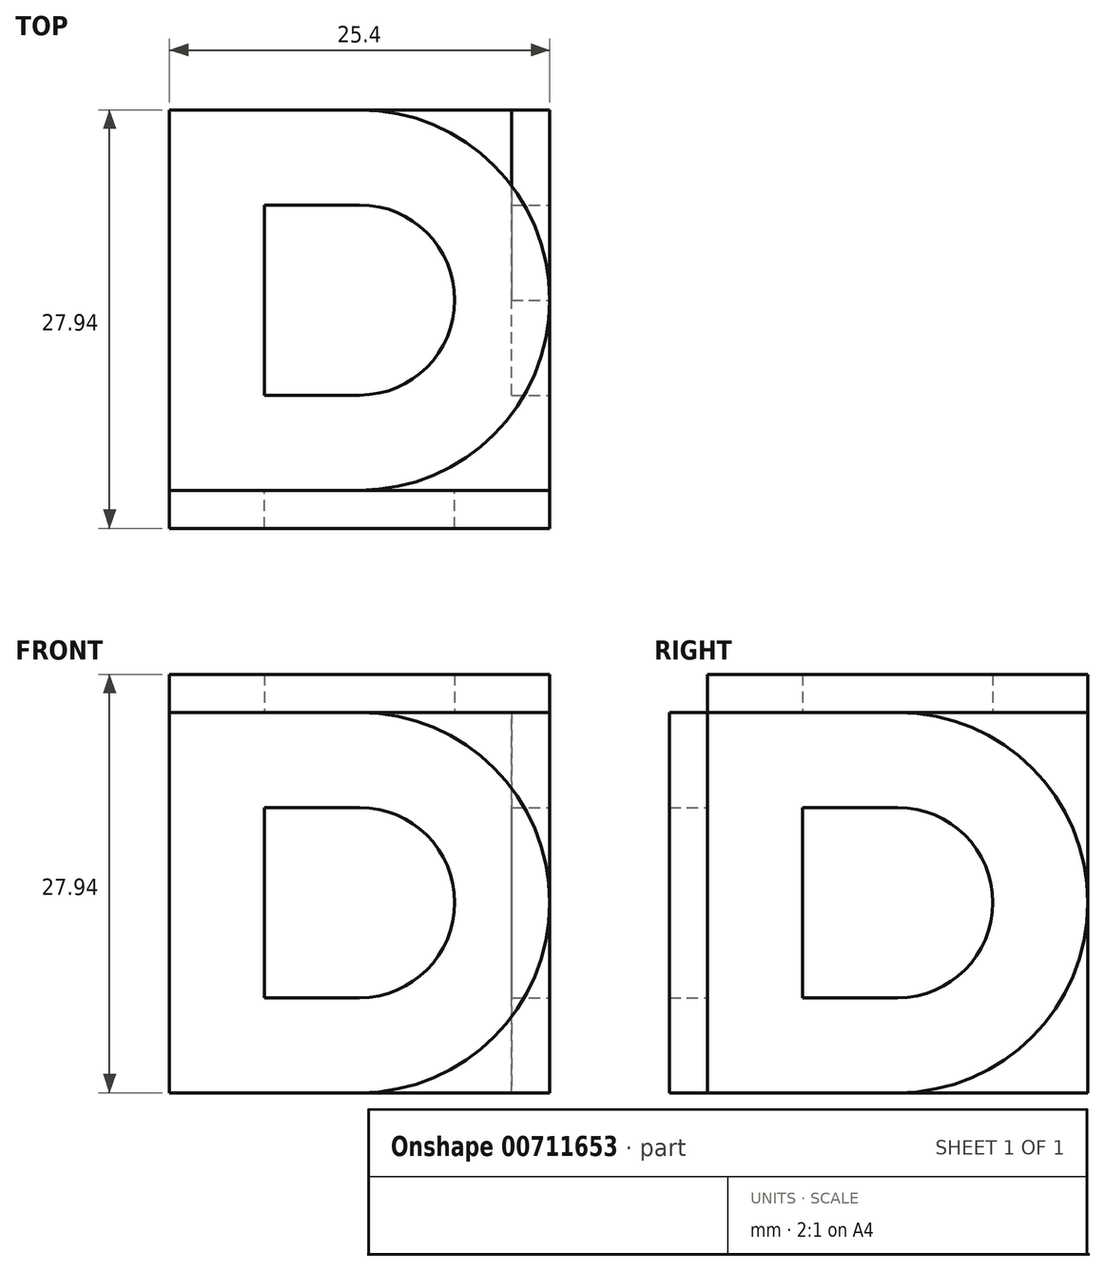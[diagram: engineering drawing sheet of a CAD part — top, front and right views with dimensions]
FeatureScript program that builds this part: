
annotation { "Feature Type Name" : "Feature", "Feature Type Description" : "" }
export const myFeature = defineFeature(function(context is Context, id is Id, definition is map)
    precondition{}
    {
        {
            var Q0;
            Q0=qCreatedBy(makeId("Top.planeOp"),FACE);
            var sketch = newSketch(context, id + "F0", { "sketchPlane" : qUnion([Q0])});
            skLineSegment(sketch, "E0.bottom", {"start": v(12.7, 12.7) * mm, "end": v(-12.7, 12.7) * mm});
            skLineSegment(sketch, "E0.top", {"start": v(12.7, -12.7) * mm, "end": v(-12.7, -12.7) * mm});
            skLineSegment(sketch, "E0.left", {"start": v(12.7, 12.7) * mm, "end": v(12.7, -12.7) * mm});
            skLineSegment(sketch, "E0.right", {"start": v(-12.7, 12.7) * mm, "end": v(-12.7, -12.7) * mm});
            skPoint(sketch, "E0.middle", {"position": v(0, 0) * mm});
            skSolve(sketch);
        }
        {
            var Q0;
            Q0 = qSketchRegion(id + "F0", true);
            extrude(context, id + "F1", {"entities" : qUnion([Q0]), "depth" : 25.4 * mm, "offsetDistance" : 25.4 * mm});
        }
        {
            var Q0;
            Q0=makeQuery(id+"F1.opExtrude","CAP_FACE",FACE,{"disambiguationData":[OSD([sQuery(id+"F0.wireOp",EDGE,"E0.bottom"),sQuery(id+"F0.wireOp",EDGE,"E0.top"),sQuery(id+"F0.wireOp",EDGE,"E0.left"),sQuery(id+"F0.wireOp",EDGE,"E0.right")])],"isStart":false});
            var sketch = newSketch(context, id + "F2", { "sketchPlane" : qUnion([Q0])});
            skLineSegment(sketch, "E1.bottom", {"start": v(0, 12.7) * mm, "end": v(-12.7, 12.7) * mm});
            skLineSegment(sketch, "E1.top", {"start": v(0, -12.7) * mm, "end": v(-12.7, -12.7) * mm});
            skLineSegment(sketch, "E1.left", {"start": v(12.7, 0) * mm, "end": v(12.7, 0) * mm});
            skLineSegment(sketch, "E1.right", {"start": v(-12.7, 12.7) * mm, "end": v(-12.7, -12.7) * mm});
            skPoint(sketch, "E1.middle", {"position": v(0, 0) * mm});
            skPoint(sketch, "E2.visualSharp", {"position": v(12.7, 12.7) * mm});
            skArc(sketch, "E2.filletArc", {"start": v(12.7, 0) * mm, "mid": v(8.98, 8.98) * mm, "end": v(0, 12.7) * mm});
            skPoint(sketch, "E3.visualSharp", {"position": v(12.7, -12.7) * mm});
            skArc(sketch, "E3.filletArc", {"start": v(0, -12.7) * mm, "mid": v(8.98, -8.98) * mm, "end": v(12.7, 0) * mm});
            skLineSegment(sketch, "E4.0", {"start": v(-6.35, 6.35) * mm, "end": v(-6.35, -6.35) * mm});
            skLineSegment(sketch, "E4.1", {"start": v(0, -6.35) * mm, "end": v(-6.35, -6.35) * mm});
            skLineSegment(sketch, "E4.2", {"start": v(0, 6.35) * mm, "end": v(-6.35, 6.35) * mm});
            skArc(sketch, "E4.3", {"start": v(6.35, 0) * mm, "mid": v(4.5, 4.5) * mm, "end": v(0, 6.35) * mm});
            skArc(sketch, "E4.4", {"start": v(0, -6.35) * mm, "mid": v(4.5, -4.5) * mm, "end": v(6.35, 0) * mm});
            skSolve(sketch);
        }
        {
            var Q0;
            Q0=makeQuery(id+"F1.opExtrude","SWEPT_FACE",FACE,{"disambiguationData":[OSD([sQuery(id+"F0.wireOp",EDGE,"E0.top")])]});
            var sketch = newSketch(context, id + "F3", { "sketchPlane" : qUnion([Q0])});
            skLineSegment(sketch, "E5.bottom", {"start": v(-12.7, 0) * mm, "end": v(0, 0) * mm});
            skLineSegment(sketch, "E5.top", {"start": v(-12.7, 25.4) * mm, "end": v(0, 25.4) * mm});
            skLineSegment(sketch, "E5.left", {"start": v(-12.7, 0) * mm, "end": v(-12.7, 25.4) * mm});
            skLineSegment(sketch, "E5.right", {"start": v(12.7, 12.7) * mm, "end": v(12.7, 12.7) * mm});
            skPoint(sketch, "E6.visualSharp", {"position": v(12.7, 25.4) * mm});
            skArc(sketch, "E6.filletArc", {"start": v(12.7, 12.7) * mm, "mid": v(8.98, 21.68) * mm, "end": v(0, 25.4) * mm});
            skPoint(sketch, "E7.visualSharp", {"position": v(12.7, 0) * mm});
            skArc(sketch, "E7.filletArc", {"start": v(0, 0) * mm, "mid": v(8.98, 3.72) * mm, "end": v(12.7, 12.7) * mm});
            skLineSegment(sketch, "E8.0", {"start": v(0, 19.05) * mm, "end": v(-6.35, 19.05) * mm});
            skArc(sketch, "E8.1", {"start": v(6.35, 12.7) * mm, "mid": v(4.5, 17.2) * mm, "end": v(0, 19.05) * mm});
            skLineSegment(sketch, "E8.2", {"start": v(-6.35, 6.35) * mm, "end": v(-6.35, 19.05) * mm});
            skLineSegment(sketch, "E8.3", {"start": v(-6.35, 6.35) * mm, "end": v(0, 6.35) * mm});
            skArc(sketch, "E8.4", {"start": v(0, 6.35) * mm, "mid": v(4.5, 8.2) * mm, "end": v(6.35, 12.7) * mm});
            skSolve(sketch);
        }
        {
            var Q0;
            Q0=makeQuery(id+"F1.opExtrude","SWEPT_FACE",FACE,{"disambiguationData":[OSD([sQuery(id+"F0.wireOp",EDGE,"E0.left")])]});
            var sketch = newSketch(context, id + "F4", { "sketchPlane" : qUnion([Q0])});
            skLineSegment(sketch, "E9.bottom", {"start": v(0, 25.4) * mm, "end": v(-12.7, 25.4) * mm});
            skLineSegment(sketch, "E9.top", {"start": v(0, 0) * mm, "end": v(-12.7, 0) * mm});
            skLineSegment(sketch, "E9.left", {"start": v(12.7, 12.7) * mm, "end": v(12.7, 12.7) * mm});
            skLineSegment(sketch, "E9.right", {"start": v(-12.7, 25.4) * mm, "end": v(-12.7, 0) * mm});
            skPoint(sketch, "E10.visualSharp", {"position": v(12.7, 25.4) * mm});
            skArc(sketch, "E10.filletArc", {"start": v(12.7, 12.7) * mm, "mid": v(8.98, 21.68) * mm, "end": v(0, 25.4) * mm});
            skPoint(sketch, "E11.visualSharp", {"position": v(12.7, 0) * mm});
            skArc(sketch, "E11.filletArc", {"start": v(0, 0) * mm, "mid": v(8.98, 3.72) * mm, "end": v(12.7, 12.7) * mm});
            skLineSegment(sketch, "E12.0", {"start": v(-6.35, 19.05) * mm, "end": v(0, 19.05) * mm});
            skArc(sketch, "E12.1", {"start": v(6.35, 12.7) * mm, "mid": v(4.5, 17.2) * mm, "end": v(0, 19.05) * mm});
            skLineSegment(sketch, "E12.2", {"start": v(-6.35, 19.05) * mm, "end": v(-6.35, 6.35) * mm});
            skLineSegment(sketch, "E12.3", {"start": v(0, 6.35) * mm, "end": v(-6.35, 6.35) * mm});
            skArc(sketch, "E12.4", {"start": v(0, 6.35) * mm, "mid": v(4.5, 8.2) * mm, "end": v(6.35, 12.7) * mm});
            skSolve(sketch);
        }
        {
            var Q0;
            Q0=makeQuery(id+"F2.imprint","IMPRINT",FACE,{"disambiguationData":[TD([[makeQuery(id+"F2.imprint","IMPRINT",EDGE,{"derivedFrom":sQuery(id+"F2.wireOp",EDGE,"E1.bottom")}),1.0]])]});
            extrude(context, id + "F5", {"entities" : qUnion([Q0]), "operationType" : NewBodyOperationType.ADD, "depth" : 2.54 * mm, "offsetDistance" : 25.4 * mm});
        }
        {
            var Q0;
            Q0=makeQuery(id+"F3.imprint","IMPRINT",FACE,{"disambiguationData":[TD([[makeQuery(id+"F3.imprint","IMPRINT",EDGE,{"derivedFrom":sQuery(id+"F3.wireOp",EDGE,"E5.bottom")}),-1.0]])]});
            extrude(context, id + "F6", {"entities" : qUnion([Q0]), "operationType" : NewBodyOperationType.ADD, "depth" : 2.54 * mm, "offsetDistance" : 25.4 * mm});
        }
        {
            var Q0;
            Q0=makeQuery(id+"F4.imprint","IMPRINT",FACE,{"disambiguationData":[TD([[makeQuery(id+"F4.imprint","IMPRINT",EDGE,{"derivedFrom":sQuery(id+"F4.wireOp",EDGE,"E12.0")}),-1.0]])]});
            var Q1;
            {var subQ0=sQuery(id+"F4.wireOp",EDGE,"E10.filletArc");Q1=makeQuery(id+"F4.imprint","IMPRINT",FACE,{"disambiguationData":[TD([[makeQuery(id+"F4.imprint","IMPRINT",EDGE,{"derivedFrom":subQ0}),-1.0]])]});}
            var Q2;
            {var subQ0=sQuery(id+"F4.wireOp",EDGE,"E11.filletArc");Q2=makeQuery(id+"F4.imprint","IMPRINT",FACE,{"disambiguationData":[TD([[makeQuery(id+"F4.imprint","IMPRINT",EDGE,{"derivedFrom":subQ0}),-1.0]])]});}
            extrude(context, id + "F7", {"entities" : qUnion([Q0, Q1, Q2]), "operationType" : NewBodyOperationType.REMOVE, "oppositeDirection" : true, "depth" : 2.54 * mm, "offsetDistance" : 25.4 * mm});
        }
    });
